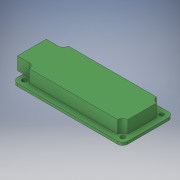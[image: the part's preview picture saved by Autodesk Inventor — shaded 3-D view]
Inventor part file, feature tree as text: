
AUTODESK INVENTOR PART (.ipt)
format: ipt  version: 2019 (Build 230136000, 136)  size: 159,232 bytes
history: native  units: mm
features: extrude x2, sketch x2
ambient origin geometry x8: Origin, YZ Plane, XZ Plane, XY Plane, X Axis, Y Axis, Z Axis, Center Point
bodies: Solid1 (feature_tree)
feature tree (4):
  extrude  "Extrusion1"  Depth=30.0mm
  extrude  "Extrusion3"  Depth=7.5mm
  sketch  "Sketch1"  dims[d0=65.0mm d1=30.0mm]
  sketch  "Sketch2"  dims[d2=3.0mm d3=2.5mm d4=3.5mm d5=3.5mm d6=20.0mm d8=23.0mm d9=20.0mm d11=58.0mm d14=1.6mm d15=0.0mm d17=6.0mm d18=20.0mm d20=23.0mm d21=20.0mm d23=58.0mm d28=7.0mm d29=7.0mm d30=7.5mm d31=0.0mm]
